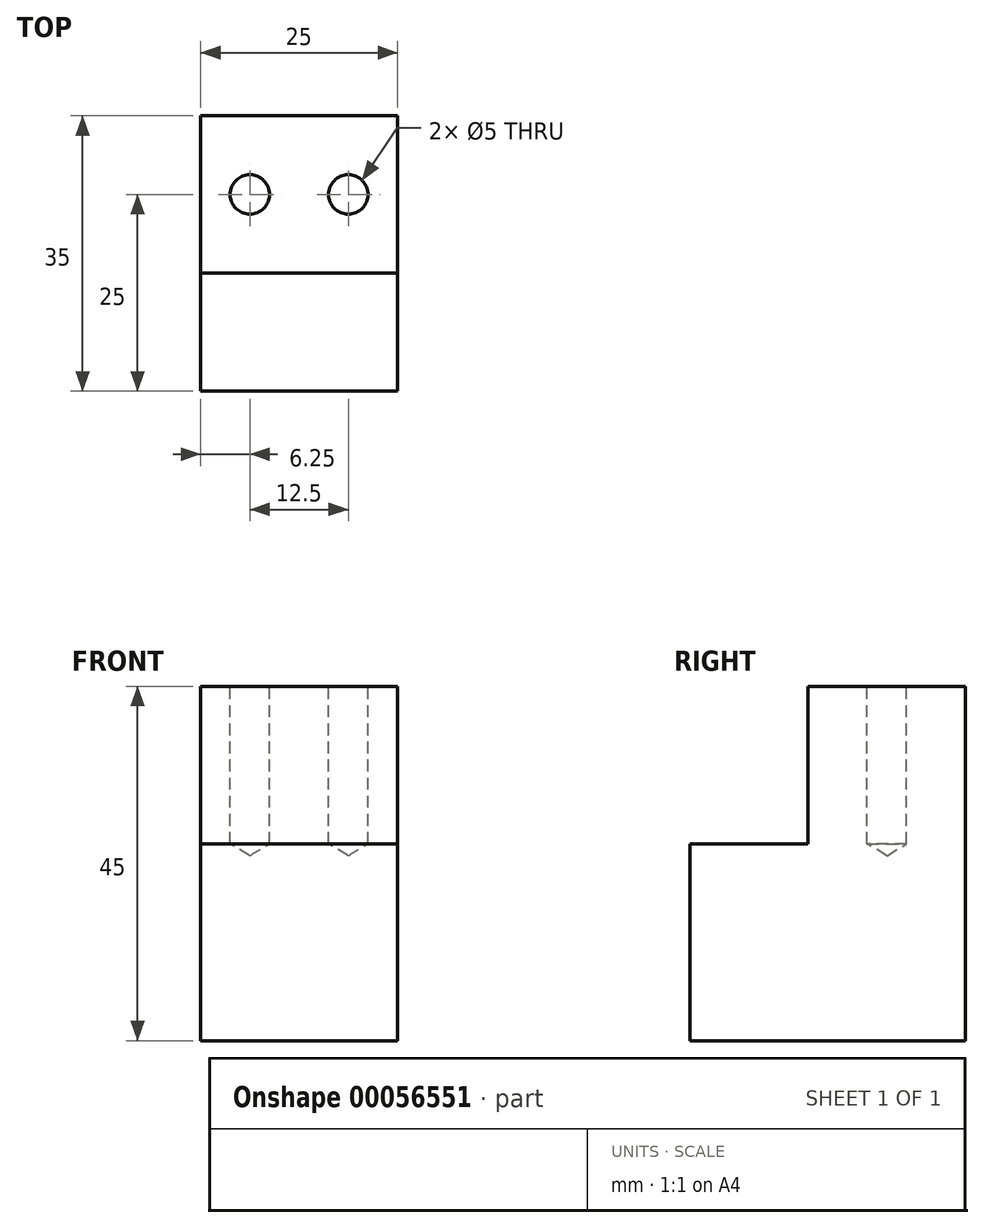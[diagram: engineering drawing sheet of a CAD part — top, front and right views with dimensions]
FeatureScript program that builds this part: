
annotation { "Feature Type Name" : "Feature", "Feature Type Description" : "" }
export const myFeature = defineFeature(function(context is Context, id is Id, definition is map)
    precondition{}
    {
        {
            var Q0;
            Q0=qCreatedBy(makeId("Top.planeOp"),FACE);
            var sketch = newSketch(context, id + "F0", { "sketchPlane" : qUnion([Q0])});
            skLineSegment(sketch, "E0", {"start": v(0, 0) * mm, "end": v(0, 35) * mm});
            skLineSegment(sketch, "E1", {"start": v(0, 35) * mm, "end": v(25, 35) * mm});
            skLineSegment(sketch, "E2", {"start": v(25, 35) * mm, "end": v(25, 0) * mm});
            skLineSegment(sketch, "E3", {"start": v(25, 0) * mm, "end": v(0, 0) * mm});
            skSolve(sketch);
        }
        {
            var Q0;
            Q0 = qSketchRegion(id + "F0", true);
            var Q1;
            Q1 = qConstructionFilter(qBodyType(qCreatedBy(id + "F0" ,EDGE), BodyType.WIRE), ConstructionObject.NO);
            extrude(context, id + "F1", {"entities" : qUnion([Q0]), "surfaceEntities" : qUnion([Q1]), "depth" : 25 * mm});
        }
        {
            var Q0;
            Q0=makeQuery(id+"F1.opExtrude","SWEPT_FACE",FACE,{"disambiguationData":[OSD([sQuery(id+"F0.wireOp",EDGE,"E2")])]});
            var sketch = newSketch(context, id + "F2", { "sketchPlane" : qUnion([Q0])});
            skLineSegment(sketch, "E4.bottom", {"start": v(35, 25) * mm, "end": v(15, 25) * mm});
            skLineSegment(sketch, "E4.top", {"start": v(35, 45) * mm, "end": v(15, 45) * mm});
            skLineSegment(sketch, "E4.left", {"start": v(35, 25) * mm, "end": v(35, 45) * mm});
            skLineSegment(sketch, "E4.right", {"start": v(15, 25) * mm, "end": v(15, 45) * mm});
            skSolve(sketch);
        }
        {
            var Q0;
            Q0 = qSketchRegion(id + "F2", true);
            extrude(context, id + "F3", {"entities" : qUnion([Q0]), "operationType" : NewBodyOperationType.ADD, "oppositeDirection" : true, "depth" : 25 * mm});
        }
        {
            var Q0;
            Q0=makeQuery(id+"F3.opExtrude","SWEPT_FACE",FACE,{"disambiguationData":[OSD([sQuery(id+"F2.wireOp",EDGE,"E4.top")])]});
            var sketch = newSketch(context, id + "F4", { "sketchPlane" : qUnion([Q0])});
            skPoint(sketch, "E5", {"position": v(6.25, 25) * mm});
            skPoint(sketch, "E6", {"position": v(18.75, 25) * mm});
            skLineSegment(sketch, "E7", {"start": v(0, 15) * mm, "end": v(12.5, 35) * mm});
            skLineSegment(sketch, "E8", {"start": v(12.5, 35) * mm, "end": v(25, 15) * mm});
            skSolve(sketch);
        }
        {
            var Q0;
            Q0=sQuery(id+"F4.wireOp",VERTEX,"E5");
            var Q1;
            Q1=sQuery(id+"F4.wireOp",VERTEX,"E6");
            var Q2;
            Q2=makeQuery(id+"F1.opExtrude","SWEPT_BODY",BODY,{"disambiguationData":[OSD([sQuery(id+"F0.wireOp",EDGE,"E0"),sQuery(id+"F0.wireOp",EDGE,"E1"),sQuery(id+"F0.wireOp",EDGE,"E2"),sQuery(id+"F0.wireOp",EDGE,"E3")])]});
            hole(context, id + "F5", {"style" : HoleStyle.SIMPLE, "holeDiameter" : 5 * mm, "endStyle" : HoleEndStyle.BLIND, "holeDepth" : 20 * mm, "locations" : qUnion([Q0, Q1]), "scope" : qUnion([Q2])});
        }
    });
